# Revit family: ZDF
name_source: partatom
category: Mechanical Equipment
revit_build: Autodesk Revit 2017 (Build: 20160606_1515(x64)
units: mm (PartAtom-declared; Revit-internal decimal feet)

## family parameters
Always vertical = Yes
Cut with Voids When Loaded = No
OmniClass Number = 23.75.00.00
OmniClass Title = Climate Control (HVAC)
Part Type = Normal
Room Calculation Point = No
Round Connector Dimension = Use Diameter
Shared = No
Work Plane-Based = No

## types (1)
- ZDF - 536/355/457
    Accessories = https://www.assaabloyglobalsolutions.com
    Article Number = 'Locks needs to be configured *
    Assembly Country = China
    BIM Group ID = ZDF
    Brand = Elsafe
    CB Certificate = https://assaabloy.box.com
    Date of publishing = V1.01
    Depth(mm) = 457 mm  [stored 1.49934 ft]
    Description = Elsafe Zenith Digital Floor Safe. Size 536x355x457mm. Internal volume: 66 litres. With or without a drop slope solution. With 3 different body, frame and front colours: black/grey RAL7021, ivory RAL1015,white RAL9003. Weight 36,2 kilos.
    Design Country = Scandinavia
    DoC = https://assaabloy.box.com
    EDP Declaration = https://assaabloy.box.com
    Environmental Management System ISO14001 - EMS 596620 = https://www.assaabloyglobalsolutions.com
    Finish = https://www.assaabloyglobalsolutions.com
    General = 10/2/2020
    Height(mm) = 536 mm
    ISO45001 - OHS596621 = https://www.assaabloyglobalsolutions.com
    ISO9001 - FM597854 = https://www.assaabloyglobalsolutions.com
    Main Material = Steel
    Manufacturer = ASSA ABLOY
    Manufacturing Country = China
    NEMKO (EMC) = https://assaabloy.box.com
    Name = Elsafe Zenith Floor Safe
    Product Datasheet = https://www.assaabloyglobalsolutions.com
    Product Group = Electronic Safes
    Product Range = Zenith
    Provider = ASSA ABLOY Global Solutions
    Region = Global
    Secondary Material = Polycarbonate
    Similar products from ASSA ABLOY Global Solutions = https://www.assaabloyglobalsolutions.com
    UL Reference Standards = Connect to https://iq.ulprospector.com , create a user FOC and search for ASSA ABLOY Global Solutions to see all our files (i.e the file called GYQS.R19020, you will find our locks and their fire approvals)
    Weight(KG) = 36
    Width(mm) = 355 mm

note: [stored X ft] marks values corroborated as IEEE doubles in the binary element streams (Revit-internal decimal feet)

## geometry (parser evidence)
native form markers: Sweep x2
no freeform markers — native parametric forms only
